# Revit family: Shades-Hunter_Douglas-RB500-Single_Standard_Duty-Clutch-38_46_55_Bracket-Pocket-tw82-ky
name_source: partatom
category: Specialty Equipment
units: mm (PartAtom-declared; Revit-internal decimal feet)

## family parameters
Always vertical = Yes
Cut with Voids When Loaded = No
OmniClass Number = 23.30.60.14
OmniClass Title = Interior Window Treatment
Part Type = Normal
Room Calculation Point = No
Round Connector Dimension = Use Diameter
Shared = No
Work Plane-Based = No

## types (9) — shared parameters
Assembly Code = E2010300
CD_Fabric Sizing Disclaimer = Designer to verify maximum fabric size with Manufacturer as the maximum fabric size is dependent on finished dimensions
CD_Finish = Fabric-Shade-Hunter_Douglas-5%-E_Screen-Charcoal_Cocoa
CD_Finish Frame = Metal-Aluminum-Hunter_Douglas-Anodized-White
CD_Finish Rail = Metal-Aluminum-Hunter_Douglas-Anodized-White
CD_Install Documentation = https://www.hunterdouglasarchitectural.com
CD_Microsite = https://microsite.caddetails.com
CD_Product Documentation Link = https://www.hunterdouglasarchitectural.com
CD_Product Name = RB 500 Roller Shade System
CD_Product Page URL = https://www.hunterdouglasarchitectural.com
CD_Roller Offset = 0' - 2 21/32"
CD_Screen Offset From Face = 0' - 1 3/8"
CD_Warranty = https://assets.hunterdouglasarchitectural.com
Description = Standard Duty Clutch Roller Shade
Manufacturer = Hunter Douglas Architectural
URL = https://www.hunterdouglasarchitectural.com

## per-type parameters (varying)
| type | CD_38 | CD_46 | CD_55 | CD_Base Gypsum Offset | CD_Bottom Offset | CD_Bracket Depth | CD_Bracket Height | CD_Front Gypsum Offset | CD_Gypsum Pocket | CD_Gypsum Pocket 38 | CD_Gypsum Pocket 46 | CD_Gypsum Pocket 55 | CD_Horizontal Roller Offset | CD_Surface Pocket | CD_Surface Pocket 38 | CD_Surface Pocket 46 | CD_Surface Pocket 55 | CD_Surface Pocket Calc | CD_Tile Pocket | CD_Top Bracket Offset | Model | Type Comments |
| 38 Gypsum Pocket | Yes | No | No | 0' - 0" | -0' - 0 3/16" | 0' - 5" | 0' - 5" | 0' - 0 5/32" | Yes | Yes | No | No | 0' - 3 3/8" | No | No | No | No | No | No | 0' - 0" | Standard Duty Automated 55 Bracket | Gypsum Pocket |
| 38 Tile Pocket | Yes | No | No | 0' - 0" | 0' - 0 3/32" | 0' - 5 9/32" | 0' - 5 9/32" | 0' - 0" | No | No | No | No | 0' - 3 9/16" | No | Yes | No | No | Yes | Yes | 0' - 0 3/32" | Standard Duty Automated 55 Bracket | Tile Pocket |
| 38 Surface Pocket | Yes | No | No | 0' - 0" | 0' - 0 3/32" | 0' - 5 9/32" | 0' - 5 9/32" | 0' - 0" | No | No | No | No | 0' - 3 9/16" | Yes | Yes | No | No | Yes | No | 0' - 0 3/32" | Standard Duty Automated 55 Bracket | Surface Pocket |
| 46 Surface Pocket | No | Yes | No | 0' - 0" | 0' - 0 3/32" | 0' - 5 9/32" | 0' - 5 9/32" | 0' - 0" | No | No | No | No | 0' - 3 15/32" | Yes | No | Yes | No | Yes | No | 0' - 0 3/32" | Standard Duty Automated 46 Bracket | Surface Pocket |
| 55 Surface Pocket | No | No | Yes | 0' - 0" | 0' - 0 3/32" | 0' - 5 9/32" | 0' - 5 9/32" | 0' - 0" | No | No | No | No | 0' - 3 1/16" | Yes | No | No | Yes | Yes | No | 0' - 0 3/32" | Standard Duty Clutch 55 Bracket | Surface Pocket |
| 46 Gypsum Pocket | No | Yes | No | 0' - 0 3/32" | -0' - 0 3/16" | 0' - 5" | 0' - 5" | 0' - 0 5/32" | Yes | No | Yes | No | 0' - 3 9/32" | No | No | No | No | No | No | 0' - 0" | Standard Duty Automated 46 Bracket | Gypsum Pocket |
| 55 Gypsum Pocket | No | No | Yes | 0' - 0 3/32" | -0' - 0 3/16" | 0' - 5" | 0' - 5" | 0' - 0 5/32" | Yes | No | No | Yes | 0' - 2 7/8" | No | No | No | No | No | No | 0' - 0" | Standard Duty Clutch 55 Bracket | Gypsum Pocket |
| 46 Tile Pocket | No | Yes | No | 0' - 0" | 0' - 0 3/32" | 0' - 5 9/32" | 0' - 5 9/32" | 0' - 0" | No | No | No | No | 0' - 3 15/32" | No | No | Yes | No | Yes | Yes | 0' - 0 3/32" | Standard Duty Automated 46 Bracket | Tile Pocket |
| 55 Tile Pocket | No | No | Yes | 0' - 0" | 0' - 0 3/32" | 0' - 5 9/32" | 0' - 5 9/32" | 0' - 0" | No | No | No | No | 0' - 3 1/16" | No | No | No | Yes | Yes | Yes | 0' - 0 3/32" | Standard Duty Clutch 55 Bracket | Tile Pocket |

## geometry (parser evidence)
native form markers: Sweep x3
no freeform markers — native parametric forms only
